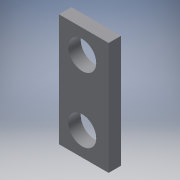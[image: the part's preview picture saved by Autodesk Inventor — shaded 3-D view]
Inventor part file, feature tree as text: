
AUTODESK INVENTOR PART (.ipt)
format: ipt  version: 2016 (Build 200138000, 138)  size: 102,912 bytes
history: native  units: in
note: dims shown in document units (in); Inventor stores cm internally (conversion verified against a paired STEP export)
features: reference x2, extrude x1, sketch x1
ambient origin geometry x8: Origin, YZ Plane, XZ Plane, XY Plane, X Axis, Y Axis, Z Axis, Center Point
bodies: Solid1 (feature_tree)
feature tree (4):
  extrude  "Extrusion1"  Depth=0.0787in
  sketch  "Sketch1"  dims[d0=0.1772in d1=0.1772in d2=0.0787in d3=0.315in d4=0.0787in d5=0.0in]
  reference  "Reference1"
  reference  "Reference2"
